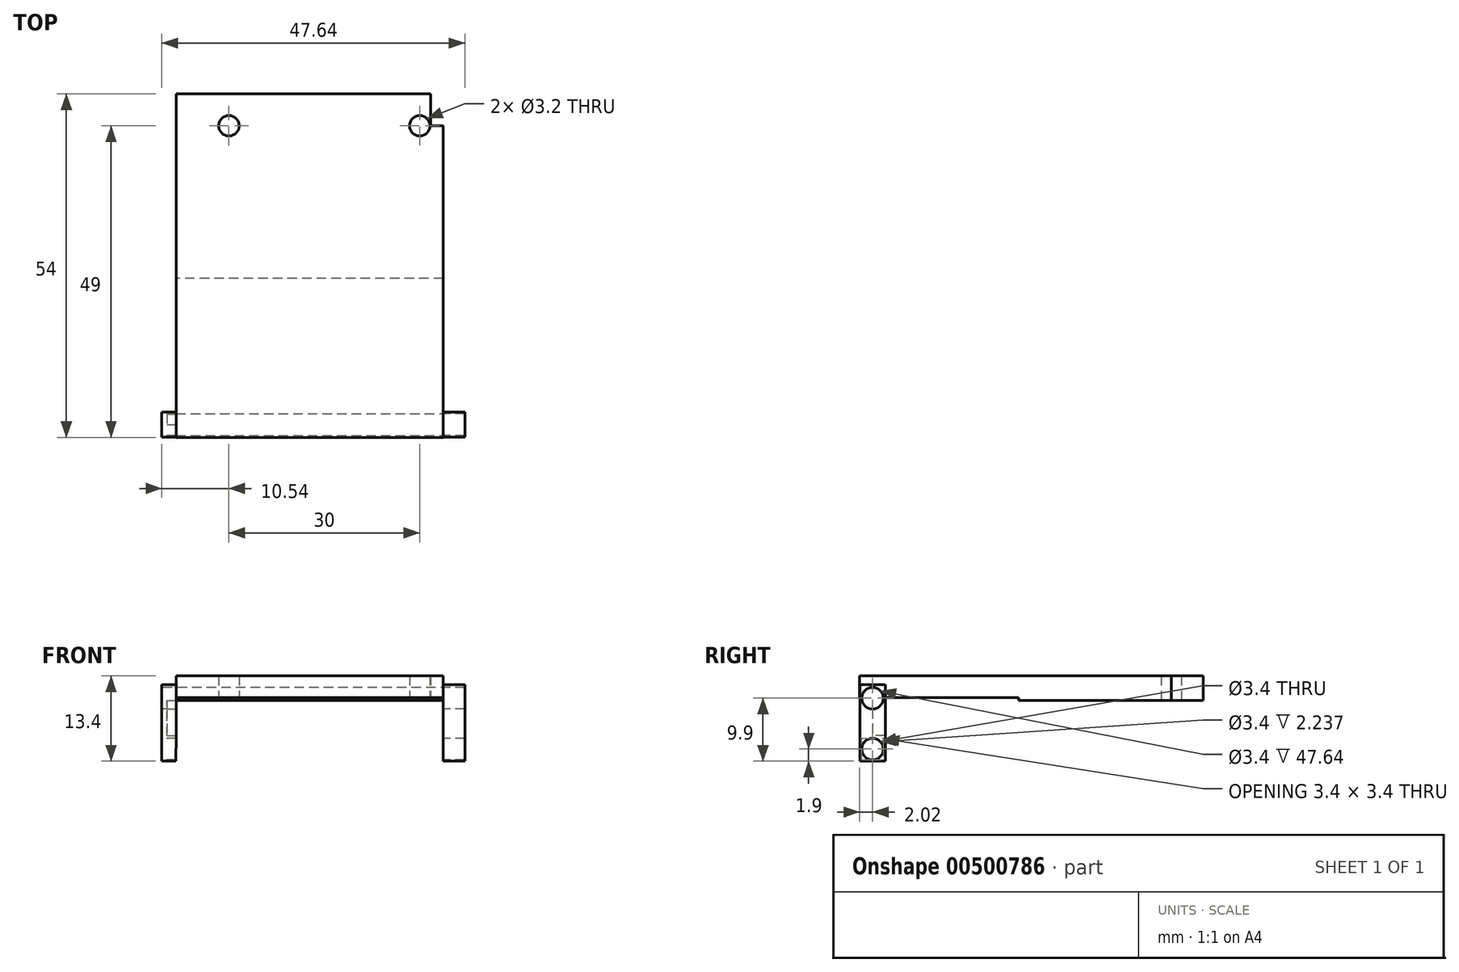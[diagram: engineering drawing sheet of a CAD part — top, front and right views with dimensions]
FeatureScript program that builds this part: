
annotation { "Feature Type Name" : "Feature", "Feature Type Description" : "" }
export const myFeature = defineFeature(function(context is Context, id is Id, definition is map)
    precondition{}
    {
        {
            var Q0;
            Q0=qCreatedBy(makeId("Right.planeOp"),FACE);
            var sketch = newSketch(context, id + "F0", { "sketchPlane" : qUnion([Q0])});
            skLineSegment(sketch, "E0.bottom", {"start": v(-2, 4) * mm, "end": v(2, 4) * mm});
            skLineSegment(sketch, "E0.top", {"start": v(-2, -4) * mm, "end": v(2, -4) * mm});
            skLineSegment(sketch, "E0.left", {"start": v(-2, 4) * mm, "end": v(-2, -4) * mm});
            skLineSegment(sketch, "E0.right", {"start": v(2, 4) * mm, "end": v(2, -4) * mm});
            skPoint(sketch, "E0.middle", {"position": v(0, 0) * mm});
            skLineSegment(sketch, "E1", {"start": v(0, -4) * mm, "end": v(0, -3.6) * mm});
            skPoint(sketch, "E1.endSnap0", {"position": v(0, -4) * mm});
            skLineSegment(sketch, "E2", {"start": v(0, -3.6) * mm, "end": v(0, -2.1) * mm});
            skCircle(sketch, "E3", {"center": v(0, -2.1) * mm, "radius": 1.7 * mm});
            skLineSegment(sketch, "E4", {"start": v(0, 4) * mm, "end": v(0, 5.9) * mm});
            skPoint(sketch, "E4.endSnap0", {"position": v(0, 4) * mm});
            skCircle(sketch, "E5", {"center": v(0, 5.9) * mm, "radius": 1.7 * mm});
            skLineSegment(sketch, "E6", {"start": v(-2, 4) * mm, "end": v(-2, 8) * mm});
            skLineSegment(sketch, "E7", {"start": v(2, 4) * mm, "end": v(2, 8) * mm});
            skLineSegment(sketch, "E8", {"start": v(2, 8) * mm, "end": v(-2, 8) * mm});
            skSolve(sketch);
        }
        {
            var Q0;
            {var subQ3=sQuery(id+"F0.wireOp",EDGE,"E0.left");Q0=makeQuery(id+"F0.imprint","IMPRINT",FACE,{"disambiguationData":[TD([[makeQuery(id+"F0.imprint","IMPRINT",EDGE,{"derivedFrom":subQ3}),1.0]])]});}
            var Q1;
            Q1=makeQuery(id+"F0.imprint","IMPRINT",FACE,{"disambiguationData":[TD([[makeQuery(id+"F0.imprint","IMPRINT",EDGE,{"derivedFrom":sQuery(id+"F0.wireOp",EDGE,"E5")}),-1.0]])]});
            extrude(context, id + "F1", {"entities" : qUnion([Q0, Q1]), "depth" : 3.4 * mm, "offsetDistance" : 25 * mm});
        }
        {
            var Q0;
            Q0=qCreatedBy(makeId("Top.planeOp"),FACE);
            var sketch = newSketch(context, id + "F2", { "sketchPlane" : qUnion([Q0])});
            skLineSegment(sketch, "E9.top", {"start": v(0, -2.02) * mm, "end": v(-42, -2.02) * mm});
            skLineSegment(sketch, "E9.left", {"start": v(0, 1.98) * mm, "end": v(0, -2.02) * mm});
            skLineSegment(sketch, "E9.right", {"start": v(-42, 1.98) * mm, "end": v(-42, -2.02) * mm});
            skLineSegment(sketch, "E10", {"start": v(0, 1.98) * mm, "end": v(0, 51.98) * mm});
            skLineSegment(sketch, "E11", {"start": v(-42, 1.98) * mm, "end": v(-42, 51.98) * mm});
            skLineSegment(sketch, "E12", {"start": v(-42, 51.98) * mm, "end": v(0, 51.98) * mm});
            skLineSegment(sketch, "E13", {"start": v(0, 51.98) * mm, "end": v(-2, 51.98) * mm});
            skLineSegment(sketch, "E14", {"start": v(-2, 51.98) * mm, "end": v(-2, 46.98) * mm});
            skLineSegment(sketch, "E15", {"start": v(-2, 46.98) * mm, "end": v(-3.7, 46.98) * mm});
            skCircle(sketch, "E16", {"center": v(-3.7, 46.98) * mm, "radius": 1.6 * mm});
            skLineSegment(sketch, "E17", {"start": v(-3.7, 46.98) * mm, "end": v(-3.7, 51.98) * mm});
            skLineSegment(sketch, "E18", {"start": v(-2, 46.98) * mm, "end": v(0, 46.98) * mm});
            skLineSegment(sketch, "E19", {"start": v(-3.7, 46.98) * mm, "end": v(-33.7, 46.98) * mm});
            skCircle(sketch, "E20", {"center": v(-33.7, 46.98) * mm, "radius": 1.6 * mm});
            skSolve(sketch);
        }
        {
            var Q0;
            Q0=makeQuery(id+"F2.imprint","IMPRINT",FACE,{"disambiguationData":[TD([[makeQuery(id+"F2.imprint","IMPRINT",EDGE,{"derivedFrom":sQuery(id+"F2.wireOp",EDGE,"E9.top")}),-1.0]])]});
            var Q1;
            {var subQ0=sQuery(id+"F2.wireOp",EDGE,"E14");Q1=makeQuery(id+"F2.imprint","IMPRINT",FACE,{"disambiguationData":[TD([[makeQuery(id+"F2.imprint","IMPRINT",EDGE,{"derivedFrom":subQ0}),-1.0]])]});}
            var Q2;
            {var subQ6=sQuery(id+"F2.wireOp",EDGE,"E13");Q2=makeQuery(id+"F2.imprint","IMPRINT",FACE,{"disambiguationData":[TD([[makeQuery(id+"F2.imprint","IMPRINT",EDGE,{"derivedFrom":subQ6}),1.0]])]});}
            var Q3;
            {var subQ1=sQuery(id+"F2.wireOp",EDGE,"CbIFOYgo-VhMP-dGGI-lVX8-0ayef9R9Ij01");var subQ5=sQuery(id+"F2.wireOp",EDGE,"E14");var subQ6=makeQuery(id+"F2.imprint","INTERSECT",VERTEX,{"derivedFrom":[subQ1,subQ5]});Q3=makeQuery(id+"F2.imprint","IMPRINT",FACE,{"disambiguationData":[TD([[makeQuery(id+"F2.imprint","IMPRINT",EDGE,{"disambiguationData":[TD([[subQ6,-1.0]])],"derivedFrom":subQ1}),-1.0]])]});}
            extrude(context, id + "F3", {"entities" : qUnion([Q0, Q1, Q2, Q3]), "operationType" : NewBodyOperationType.ADD, "depth" : 9.4 * mm, "offsetDistance" : 25 * mm});
        }
        {
            var Q0;
            {var subQ3=sQuery(id+"F0.wireOp",EDGE,"E0.left");Q0=makeQuery(id+"F0.imprint","IMPRINT",FACE,{"disambiguationData":[TD([[makeQuery(id+"F0.imprint","IMPRINT",EDGE,{"derivedFrom":subQ3}),1.0]])]});}
            var Q1;
            Q1=makeQuery(id+"F0.imprint","IMPRINT",FACE,{"disambiguationData":[TD([[makeQuery(id+"F0.imprint","IMPRINT",EDGE,{"derivedFrom":sQuery(id+"F0.wireOp",EDGE,"E5")}),-1.0]])]});
            extrude(context, id + "F4", {"entities" : qUnion([Q0, Q1]), "operationType" : NewBodyOperationType.ADD, "oppositeDirection" : true, "depth" : 44.24 * mm, "offsetDistance" : 25 * mm});
        }
        {
            var Q0;
            Q0=qCreatedBy(makeId("Front.planeOp"),FACE);
            var sketch = newSketch(context, id + "F5", { "sketchPlane" : qUnion([Q0])});
            skLineSegment(sketch, "E21", {"start": v(0, 0) * mm, "end": v(0, 5.54) * mm});
            skLineSegment(sketch, "E22", {"start": v(0, 5.54) * mm, "end": v(-43.43, 5.54) * mm});
            skLineSegment(sketch, "E23", {"start": v(-43.43, 5.54) * mm, "end": v(-43.43, 0) * mm});
            skLineSegment(sketch, "E24", {"start": v(-43.43, 0) * mm, "end": v(0, 0) * mm});
            skSolve(sketch);
        }
        {
            var Q0;
            Q0 = qSketchRegion(id + "F5", true);
            extrude(context, id + "F6", {"entities" : qUnion([Q0]), "operationType" : NewBodyOperationType.REMOVE, "oppositeDirection" : true, "depth" : 55 * mm, "offsetDistance" : 25 * mm});
        }
        {
            var Q0;
            Q0=makeQuery(id+"F3.opExtrude","SWEPT_FACE",FACE,{"disambiguationData":[OSD([sQuery(id+"F2.wireOp",EDGE,"E9.top")])]});
            var sketch = newSketch(context, id + "F7", { "sketchPlane" : qUnion([Q0])});
            skLineSegment(sketch, "E25", {"start": v(0, 0) * mm, "end": v(0, 6) * mm});
            skLineSegment(sketch, "E26", {"start": v(0, 6) * mm, "end": v(-42, 6) * mm});
            skLineSegment(sketch, "E27", {"start": v(-42, 6) * mm, "end": v(-42, 0) * mm});
            skLineSegment(sketch, "E28", {"start": v(-42, 0) * mm, "end": v(0, 0) * mm});
            skSolve(sketch);
        }
        {
            var Q0;
            Q0=makeQuery(id+"F7.imprint","IMPRINT",FACE,{"disambiguationData":[TD([[makeQuery(id+"F7.imprint","IMPRINT",EDGE,{"derivedFrom":sQuery(id+"F7.wireOp",EDGE,"E26")}),1.0]])]});
            extrude(context, id + "F8", {"entities" : qUnion([Q0]), "operationType" : NewBodyOperationType.REMOVE, "oppositeDirection" : true, "depth" : 25 * mm, "offsetDistance" : 25 * mm});
        }
        {
            var Q0;
            Q0=sQuery(id+"F0.wireOp",VERTEX,"E5.center");
            var Q1;
            Q1=makeQuery(id+"F1.opExtrude","SWEPT_BODY",BODY,{"disambiguationData":[OSD([sQuery(id+"F0.wireOp",EDGE,"E0.top"),sQuery(id+"F0.wireOp",EDGE,"E0.left"),sQuery(id+"F0.wireOp",EDGE,"E0.right"),sQuery(id+"F0.wireOp",EDGE,"E3"),sQuery(id+"F0.wireOp",EDGE,"E5"),sQuery(id+"F0.wireOp",EDGE,"E6"),sQuery(id+"F0.wireOp",EDGE,"E7"),sQuery(id+"F0.wireOp",EDGE,"E8")])]});
            hole(context, id + "F9", {"style" : HoleStyle.SIMPLE, "endStyle" : HoleEndStyle.THROUGH, "holeDiameter" : 3.4 * mm, "isTappedThrough" : true, "tappedDepth" : 12 * mm, "tapClearance" : 3, "locations" : qUnion([Q0]), "scope" : qUnion([Q1])});
        }
        {
            var Q0;
            {var subQ0=sQuery(id+"F0.wireOp",EDGE,"E6");var subQ1=sQuery(id+"F0.wireOp",EDGE,"E0.left");Q0=makeQuery(id+"F4.boolean.opBoolean","MERGE",FACE,{"derivedFrom":[makeQuery(id+"F1.opExtrude","SWEPT_FACE",FACE,{"disambiguationData":[OSD([subQ1,subQ0])]}),makeQuery(id+"F4.opExtrude","SWEPT_FACE",FACE,{"disambiguationData":[OSD([subQ1,subQ0])]})]});}
            var sketch = newSketch(context, id + "F10", { "sketchPlane" : qUnion([Q0])});
            skLineSegment(sketch, "E29", {"start": v(0, 0) * mm, "end": v(0, -4) * mm});
            skLineSegment(sketch, "E30", {"start": v(0, -4) * mm, "end": v(-42.03, -4) * mm});
            skLineSegment(sketch, "E31", {"start": v(-42.03, -4) * mm, "end": v(-42, 0) * mm});
            skSolve(sketch);
        }
        {
            var Q0;
            Q0=makeQuery(id+"F10.imprint","IMPRINT",FACE,{"disambiguationData":[TD([[makeQuery(id+"F10.imprint","IMPRINT",EDGE,{"derivedFrom":sQuery(id+"F10.wireOp",EDGE,"E29")}),-1.0]])]});
            extrude(context, id + "F11", {"entities" : qUnion([Q0]), "operationType" : NewBodyOperationType.REMOVE, "oppositeDirection" : true, "depth" : 25 * mm, "offsetDistance" : 25 * mm});
        }
    });
